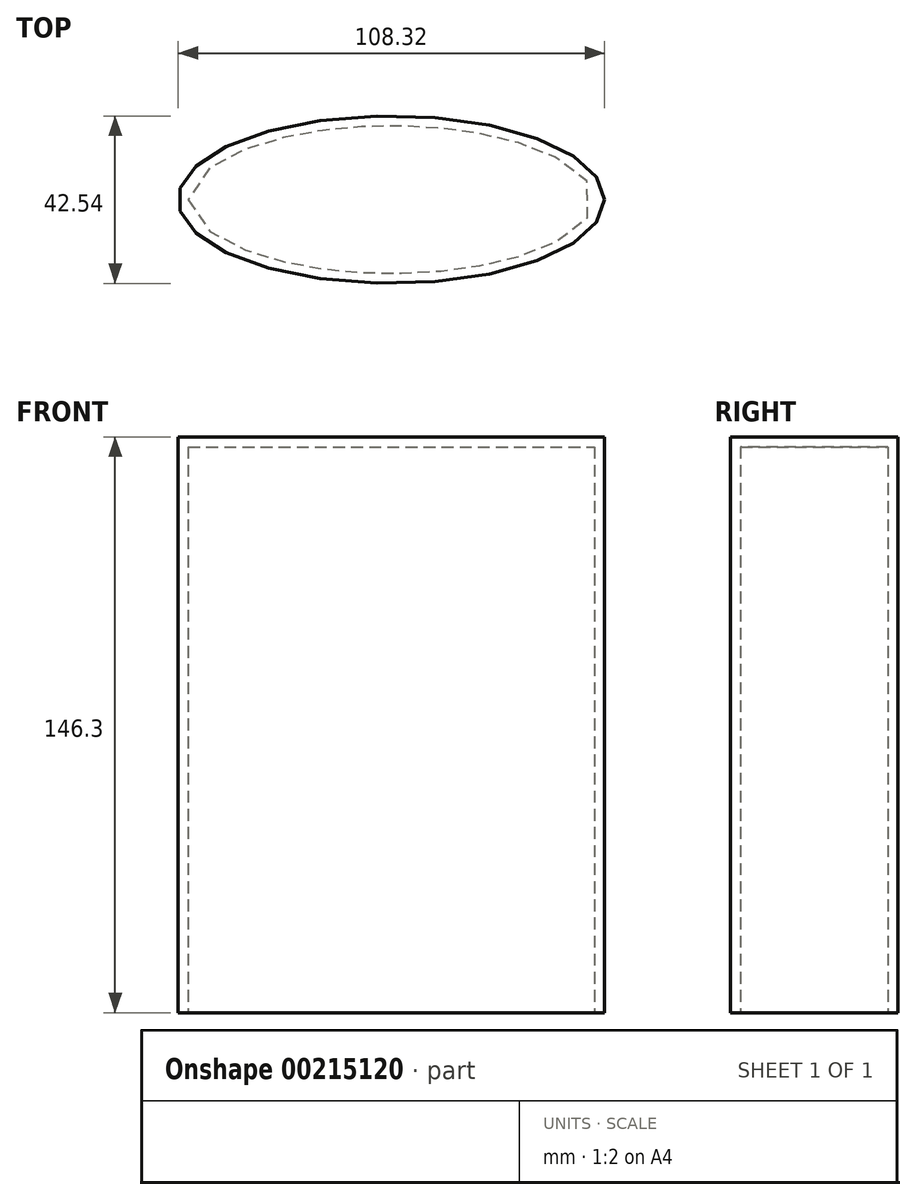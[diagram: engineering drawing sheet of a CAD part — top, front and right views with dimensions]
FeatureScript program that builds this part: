
annotation { "Feature Type Name" : "Feature", "Feature Type Description" : "" }
export const myFeature = defineFeature(function(context is Context, id is Id, definition is map)
    precondition{}
    {
        {
            var Q0;
            Q0=qCreatedBy(makeId("Top.planeOp"),FACE);
            var sketch = newSketch(context, id + "F0", { "sketchPlane" : qUnion([Q0])});
            skEllipse(sketch, "E0", {"center": v(0, 0) * mm, "majorRadius": 54.16 * mm, "minorRadius": 21.27 * mm, "majorAxis": v(1, 0)});
            skSolve(sketch);
        }
        {
            var Q0;
            Q0 = qSketchRegion(id + "F0", true);
            var Q1;
            Q1=sQuery(id+"F0.wireOp",EDGE,"E0");
            extrude(context, id + "F1", {"entities" : qUnion([Q0]), "surfaceEntities" : qUnion([Q1]), "depth" : 146.3 * mm});
        }
        {
            var Q0;
            Q0=makeQuery(id+"F1.opExtrude","CAP_FACE",FACE,{"disambiguationData":[OSD([sQuery(id+"F0.wireOp",EDGE,"E0")])],"isStart":true});
            var Q1;
            Q1=makeQuery(id+"F1.opExtrude","SWEPT_BODY",BODY,{"disambiguationData":[OSD([sQuery(id+"F0.wireOp",EDGE,"E0")])]});
            shell(context, id + "F2", {"entities" : qUnion([Q0]), "parts" : qUnion([Q1]), "thickness" : 2.54 * mm});
        }
    });
